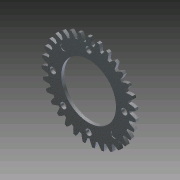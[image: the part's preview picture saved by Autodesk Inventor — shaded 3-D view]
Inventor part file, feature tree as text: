
AUTODESK INVENTOR PART (.ipt)
format: ipt  version: 2011 (Build 150239000, 239)  size: 361,984 bytes
history: native  units: mm (DEFAULTED — no unit token found)
features: sketch x6, extrude x5, plane x3, other x3, pattern_circular x2
ambient origin geometry x8: Origin, YZ Plane, XZ Plane, XY Plane, X Axis, Y Axis, Z Axis, Center Point
bodies: Solid1 (feature_tree)
feature tree (19):
  extrude  "Extrusion1"  Depth=3.175mm TaperAngle=0.0deg
  plane  "Work Plane1"
  plane  "Work Plane2"
  plane  "Work Plane3"
  other  "Spur Gear"
  extrude  "Extrusion2"  Depth=76.2mm TaperAngle=0.0deg
  extrude  "Extrusion3"  TaperAngle=0.0deg  [1 undecoded]
  pattern_circular  "Circular Pattern1"  [2 undecoded]
  pattern_circular  "Circular Pattern2"  [2 undecoded]
  extrude  "Extrusion4"  Depth=37.1475mm
  extrude  "Extrusion5"  Depth=6.35mm
  sketch  "Sketch1"  dims[d0=98.05895mm d1=3.175mm d2=0.0mm]
  sketch  "Sketch2"  dims[d3=96.02439mm d4=76.2mm d5=0.0mm]
  other  "Srf1"
  sketch  "Sketch3"  dims[d6=0.0mm d7=1.013417mm d9=0.0mm]
  sketch  "Sketch4"  dims[d14=0.0mm d15=63.5mm]
  sketch  "Sketch5"  dims[d16=0.0mm]
  sketch  "Sketch6"  dims[d17=0.0mm d18=0.0mm d19=63.5mm d20=9.525mm d21=25.4mm d22=0.0mm d23=37.1475mm d24=6.35mm d25=25.4mm d26=0.0mm d27=40.0mm d28=360.0deg d30=20.0mm d31=45.0deg d33=80.0mm d35=360.0deg d37=6.35mm d38=6.35mm d39=0.762mm d40=0.0mm d41=57.023mm d42=25.4mm d43=0.0mm]
  other  "Pitch Diameter"
note: 5 required parameter values undecoded (feature->parameter linkage not recoverable at this tier; creation-order binding heuristic only, values carry confidence <= 0.55)
